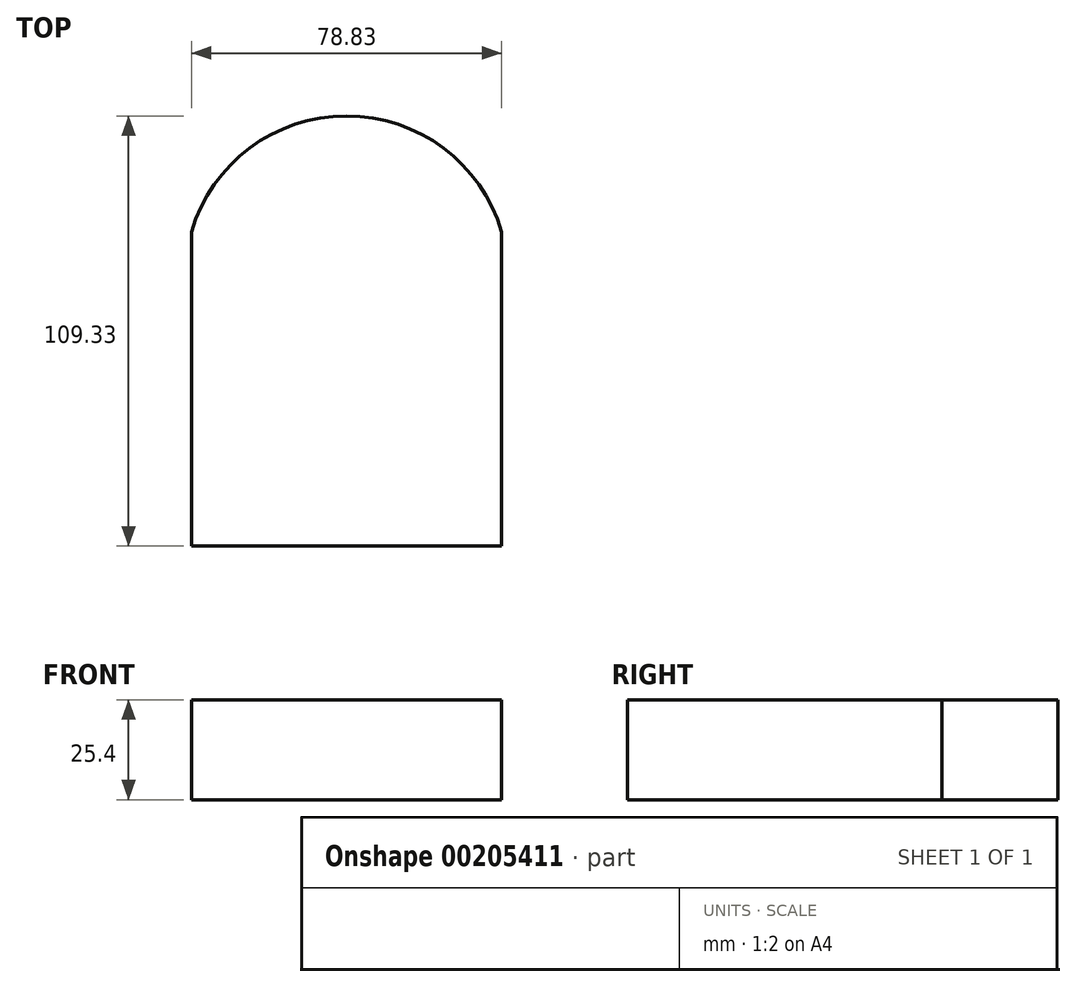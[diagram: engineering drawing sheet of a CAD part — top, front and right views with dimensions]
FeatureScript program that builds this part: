
annotation { "Feature Type Name" : "Feature", "Feature Type Description" : "" }
export const myFeature = defineFeature(function(context is Context, id is Id, definition is map)
    precondition{}
    {
        {
            var Q0;
            Q0=qCreatedBy(makeId("Top.planeOp"),FACE);
            var sketch = newSketch(context, id + "F0", { "sketchPlane" : qUnion([Q0])});
            skLineSegment(sketch, "E0.top", {"start": v(-42.37, -46.76) * mm, "end": v(36.46, -46.76) * mm});
            skLineSegment(sketch, "E0.left", {"start": v(-42.37, 33.1) * mm, "end": v(-42.37, -46.76) * mm});
            skLineSegment(sketch, "E0.right", {"start": v(36.46, 33.1) * mm, "end": v(36.46, -46.76) * mm});
            skArc(sketch, "E1", {"start": v(36.46, 33.1) * mm, "mid": v(-2.96, 62.57) * mm, "end": v(-42.37, 33.1) * mm});
            skSolve(sketch);
        }
        {
            var Q0;
            Q0 = qSketchRegion(id + "F0", true);
            extrude(context, id + "F1", {"entities" : qUnion([Q0]), "depth" : 25.4 * mm});
        }
    });
